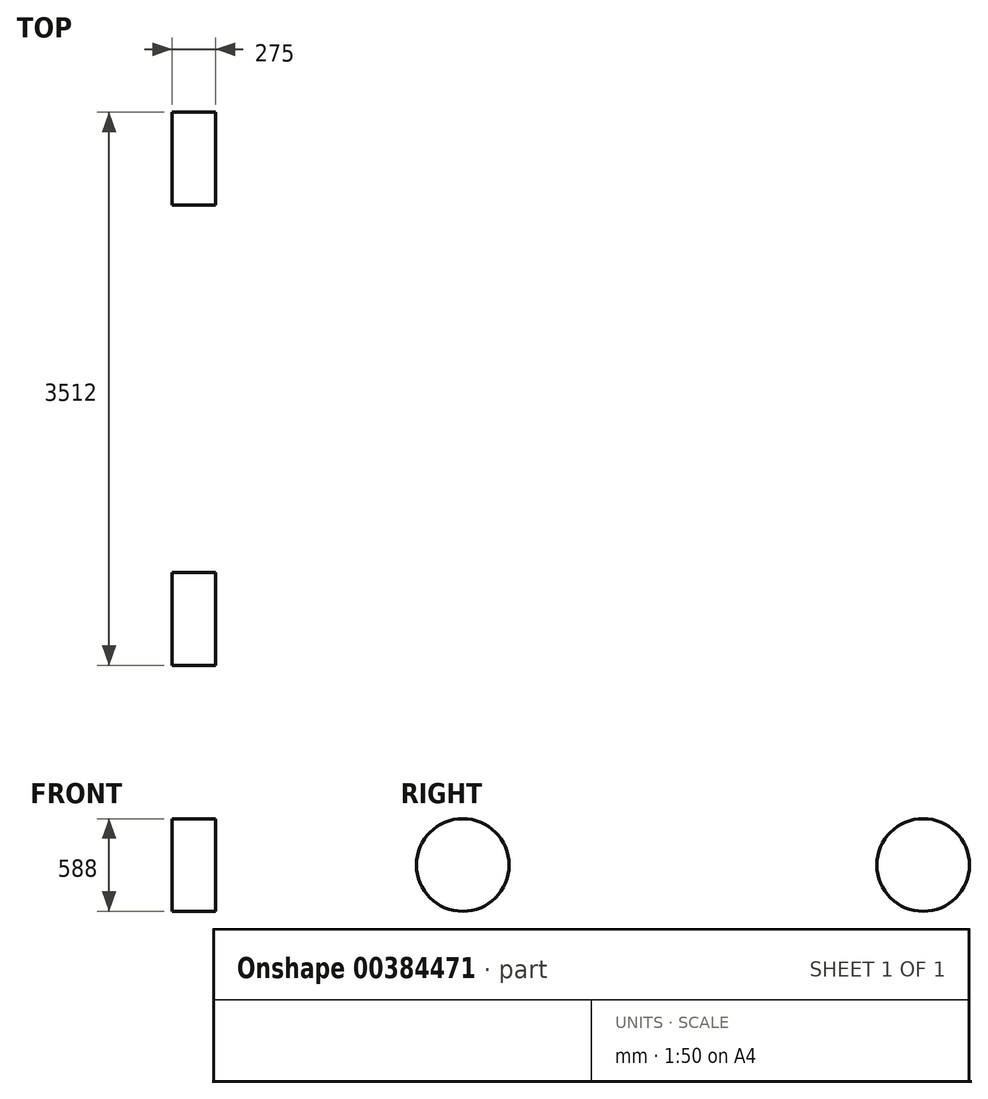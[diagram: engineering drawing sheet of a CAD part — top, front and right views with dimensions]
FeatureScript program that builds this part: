
annotation { "Feature Type Name" : "Feature", "Feature Type Description" : "" }
export const myFeature = defineFeature(function(context is Context, id is Id, definition is map)
    precondition{}
    {
        {
            var Q0;
            Q0=qCreatedBy(makeId("Right.planeOp"),FACE);
            var sketch = newSketch(context, id + "F0", { "sketchPlane" : qUnion([Q0])});
            skCircle(sketch, "E0", {"center": v(0, 0) * mm, "radius": 294 * mm});
            skLineSegment(sketch, "E1", {"start": v(0, 0) * mm, "end": v(2924, 0) * mm});
            skCircle(sketch, "E2", {"center": v(2924, 0) * mm, "radius": 294 * mm});
            skSolve(sketch);
        }
        {
            var Q0;
            Q0=sQuery(id+"F0.wireOp",EDGE,"E0");
            extrude(context, id + "F1", {"bodyType" : ToolBodyType.SURFACE, "surfaceEntities" : qUnion([Q0]), "depth" : 275 * mm});
        }
        {
            var Q0;
            Q0=sQuery(id+"F0.wireOp",EDGE,"E2");
            extrude(context, id + "F2", {"bodyType" : ToolBodyType.SURFACE, "surfaceEntities" : qUnion([Q0]), "depth" : 275 * mm});
        }
    });
